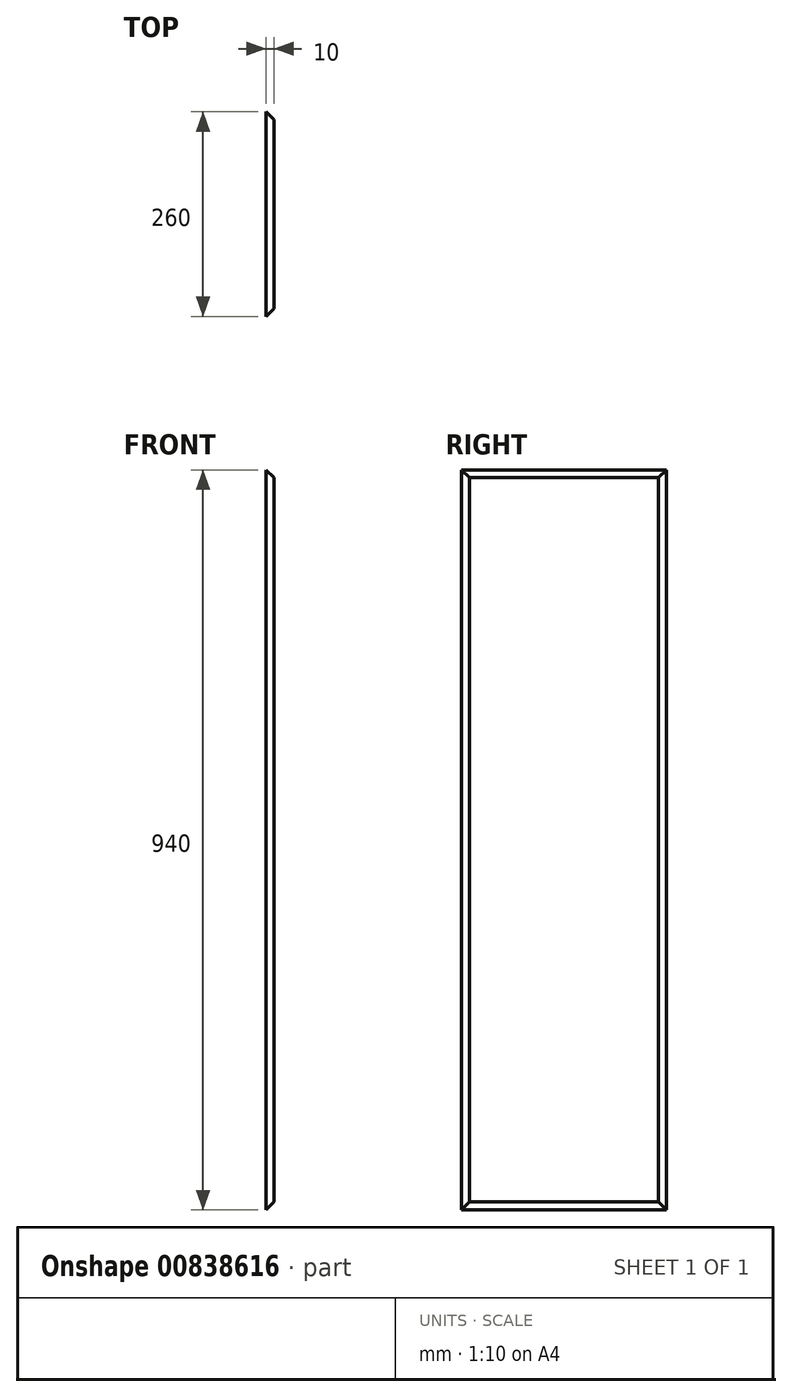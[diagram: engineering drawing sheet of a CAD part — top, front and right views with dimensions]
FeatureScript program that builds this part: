
annotation { "Feature Type Name" : "Feature", "Feature Type Description" : "" }
export const myFeature = defineFeature(function(context is Context, id is Id, definition is map)
    precondition{}
    {
        {
            var Q0;
            Q0=qCreatedBy(makeId("Right.planeOp"),FACE);
            var sketch = newSketch(context, id + "F0", { "sketchPlane" : qUnion([Q0])});
            skLineSegment(sketch, "E0.bottom", {"start": v(0, 0) * mm, "end": v(260, 0) * mm});
            skLineSegment(sketch, "E0.top", {"start": v(0, -940) * mm, "end": v(260, -940) * mm});
            skLineSegment(sketch, "E0.left", {"start": v(0, 0) * mm, "end": v(0, -940) * mm});
            skLineSegment(sketch, "E0.right", {"start": v(260, 0) * mm, "end": v(260, -940) * mm});
            skSolve(sketch);
        }
        {
            var Q0;
            Q0=makeQuery(id+"F0.imprint","IMPRINT",FACE,{"disambiguationData":[TD([[makeQuery(id+"F0.imprint","IMPRINT",EDGE,{"derivedFrom":sQuery(id+"F0.wireOp",EDGE,"E0.bottom")}),-1.0]])]});
            extrude(context, id + "F1", {"entities" : qUnion([Q0]), "endBound" : BoundingType.SYMMETRIC, "depth" : 10 * mm, "offsetDistance" : 25 * mm});
        }
        {
            var Q0;
            Q0=makeQuery(id+"F1.opExtrude","CAP_EDGE",EDGE,{"disambiguationData":[OSD([sQuery(id+"F0.wireOp",EDGE,"E0.left")])],"isStart":false});
            var Q1;
            Q1=makeQuery(id+"F1.opExtrude","CAP_EDGE",EDGE,{"disambiguationData":[OSD([sQuery(id+"F0.wireOp",EDGE,"E0.bottom")])],"isStart":false});
            var Q2;
            Q2=makeQuery(id+"F1.opExtrude","CAP_EDGE",EDGE,{"disambiguationData":[OSD([sQuery(id+"F0.wireOp",EDGE,"E0.right")])],"isStart":false});
            var Q3;
            Q3=makeQuery(id+"F1.opExtrude","CAP_EDGE",EDGE,{"disambiguationData":[OSD([sQuery(id+"F0.wireOp",EDGE,"E0.top")])],"isStart":false});
            chamfer(context, id + "F2", {"entities" : qUnion([Q0, Q1, Q2, Q3]), "width" : 10 * mm, "tangentPropagation" : true});
        }
    });
